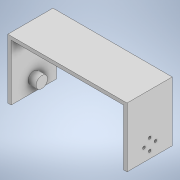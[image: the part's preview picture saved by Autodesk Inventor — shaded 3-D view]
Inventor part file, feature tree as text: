
AUTODESK INVENTOR PART (.ipt)
format: ipt  version: 2022 (Build 260153000, 153)  size: 189,440 bytes
history: native  units: mm
features: extrude x8, sketch x8
ambient origin geometry x8: Origin, YZ Plane, XZ Plane, XY Plane, X Axis, Y Axis, Z Axis, Center Point
bodies: Solid1 (feature_tree)
feature tree (16):
  extrude  "Extrusion1"  Depth=98.0mm
  extrude  "Extrusion2"  Depth=3.0mm
  extrude  "Extrusion3"  Depth=104.0mm TaperAngle=0.0deg
  extrude  "Extrusion4"  Depth=40.0mm TaperAngle=360.0deg
  extrude  "Extrusion5"  Depth=1.0mm TaperAngle=0.0deg
  extrude  "Extrusion6"  Depth=16.0mm
  extrude  "Extrusion7"  Depth=10.0mm
  extrude  "Extrusion8"  Depth=7.0mm TaperAngle=0.0deg
  sketch  "Sketch1"  dims[d0=45.0mm d1=98.0mm]
  sketch  "Sketch2"  dims[d2=3.0mm d3=48.0mm]
  sketch  "Sketch3"  dims[d4=104.0mm d5=25.4mm d6=0.0mm]
  sketch  "Sketch4"  dims[d10=2.25mm d11=40.0mm d13=360.0deg]
  sketch  "Sketch5"  dims[d15=25.4mm d16=0.0mm d17=1.0mm d18=0.0mm]
  sketch  "Sketch6"  dims[d19=4.0mm d20=0.0mm d21=16.0mm]
  sketch  "Sketch8"  dims[d22=1.0mm d23=0.0mm d26=10.0mm]
  sketch  "Sketch9"  dims[d27=7.0mm d28=0.0mm d37=7.0mm d38=0.0mm d39=7.0mm d40=0.0mm d47=0.5mm d48=0.872665mm d49=0.5mm d50=0.872665mm]
